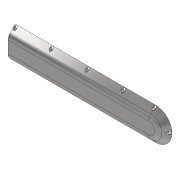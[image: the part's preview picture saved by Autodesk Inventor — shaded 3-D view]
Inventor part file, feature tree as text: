
AUTODESK INVENTOR PART (.ipt)
format: ipt  version: 2020.3 (Build 243373010, 373A)  size: 123,904 bytes
history: native  units: mm
features: extrude x1, chamfer x1, fillet x1, sketch x1
ambient origin geometry x8: Origin, YZ Plane, XZ Plane, XY Plane, X Axis, Y Axis, Z Axis, Center Point
bodies: Solid1 (feature_tree)
feature tree (4):
  extrude  "Extrusion1"  Depth=10.0mm TaperAngle=45.0deg
  chamfer  "Chamfer1"  Distance=10.0mm
  fillet  "Fillet2"  [1 undecoded]
  sketch  "Sketch2"  dims[d5=10.0mm d6=0.0mm d8=10.0mm d9=2.0mm d10=45.0deg d11=10.0mm]
note: 1 required parameter value undecoded (feature->parameter linkage not recoverable at this tier; creation-order binding heuristic only, values carry confidence <= 0.55)
